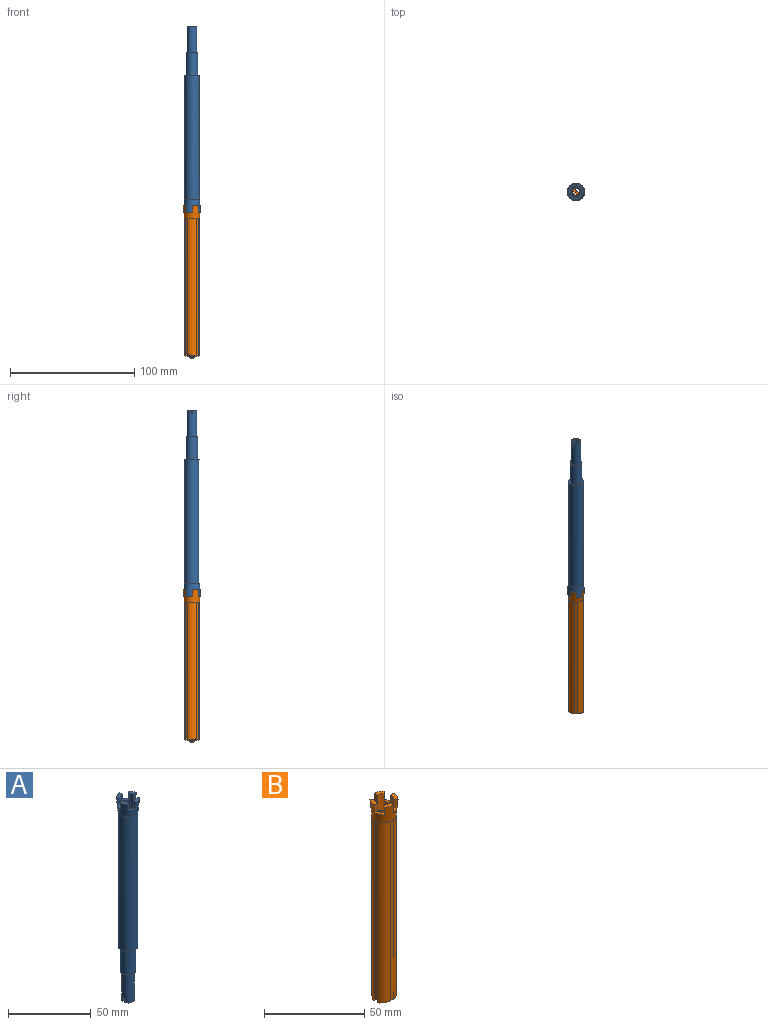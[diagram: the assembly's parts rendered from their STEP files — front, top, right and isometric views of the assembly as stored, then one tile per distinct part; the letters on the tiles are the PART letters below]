
ASSEMBLY  parts=2 mates=1
PART A: 37 faces, bbox 14x14x149.7 mm
  f0: plane 4.95x3.68mm, normal (0,0,1), area 10.6mm2, adj f3,f23,f26,f34
  f1: plane 4.96x3.68mm, normal (0,0,1), area 10.6mm2, adj f3,f23,f31,f35
  f2: plane 4.95x3.68mm, normal (0,0,1), area 10.6mm2, adj f3,f23,f28,f32
  f3: cylinder r=4.7mm len=108mm, axis (0,0,1), area 3115.5mm2, adj f0,f1,f2,f14,f24,f25,f26,f27
  f4: plane 7.63x3.1mm, normal (0,0,-1), area 8.3mm2, adj f9,f11,f16,f17
  f5: cylinder r=3.7mm len=14.3mm, axis (0,0,1), area 332.4mm2, adj f6,f14
  f6: cone r=3mm half-angle=9.9deg, axis (0,0,1), area 85.5mm2, adj f5,f11
  f7: cylinder r=4.7mm len=18.3mm, axis (0,0,-1), area 540.4mm2, adj f8,f13
  f8: plane 9.4x9.4mm, normal (0,0,-1), area 21.6mm2, adj f7,f9
  f9: cylinder r=3.9mm len=21.35mm, axis (0,0,1), area 514.1mm2, adj f4,f8,f10,f15,f16,f17,f18,f19
  f10: plane 7.63x3.1mm, normal (0,0,-1), area 8.3mm2, adj f9,f11,f15,f18
  f11: cylinder r=3mm len=19.35mm, axis (0,0,-1), area 355.6mm2, adj f4,f6,f10,f15,f16,f17,f18,f19
  f12: cylinder r=6mm len=100mm, axis (0,0,-1), area 3769.9mm2, adj f13,f23
  f13: plane 12x12mm, normal (0,0,-1), area 43.7mm2, adj f7,f12
  f14: revolved ~9.36x9.36mm, area 0mm2, adj f3,f5
  f15: plane 2.2x0.93mm, normal (0,-1,0), area 2mm2, adj f9,f10,f11,f19
  f16: plane 2.2x0.93mm, normal (0,1,0), area 2mm2, adj f4,f9,f11,f20
  f17: plane 2.2x0.93mm, normal (0,1,0), area 2mm2, adj f4,f9,f11,f21
  f18: plane 2.2x0.93mm, normal (0,-1,0), area 2mm2, adj f9,f10,f11,f22
  f19: cylinder r=0.8mm len=1.01mm, axis (-1,0,0), area 1.1mm2, adj f9,f11,f15,f20
  f20: cylinder r=0.8mm len=1.01mm, axis (-1,0,0), area 1.1mm2, adj f9,f11,f16,f19
  f21: cylinder r=0.8mm len=1.01mm, axis (-1,0,0), area 1.1mm2, adj f9,f11,f17,f22
  f22: cylinder r=0.8mm len=1.01mm, axis (-1,0,0), area 1.1mm2, adj f9,f11,f18,f21
  f23: cone r=6mm half-angle=5.7deg, axis (0,0,1), area 303.9mm2, adj f0,f1,f2,f12,f24,f25,f26,f27
  f24: plane 4.95x3.68mm, normal (0,0,1), area 10.6mm2, adj f3,f23,f25,f29
  f25: plane 5x2.3mm, normal (1,0,0), area 10.2mm2, adj f3,f23,f24,f27
  f26: plane 5x1.63mm, normal (-0.71,0.71,0), area 10.2mm2, adj f0,f3,f23,f27
  f27: plane 4.6x3.18mm, normal (0,0,1), area 7.9mm2, adj f3,f23,f25,f26
  f28: plane 5x2.3mm, normal (0,1,0), area 10.2mm2, adj f2,f3,f23,f30
  f29: plane 5x1.63mm, normal (-0.71,-0.71,0), area 10.2mm2, adj f3,f23,f24,f30
  f30: plane 4.6x3.18mm, normal (0,0,1), area 7.9mm2, adj f3,f23,f28,f29
  f31: plane 5x2.3mm, normal (-1,0,0), area 10.2mm2, adj f1,f3,f23,f33
  f32: plane 5x1.63mm, normal (0.71,-0.71,0), area 10.2mm2, adj f2,f3,f23,f33
  f33: plane 4.6x3.18mm, normal (0,0,1), area 7.9mm2, adj f3,f23,f31,f32
  f34: plane 5x2.3mm, normal (0,-1,0), area 10.2mm2, adj f0,f3,f23,f36
  f35: plane 5x1.63mm, normal (0.71,0.71,0), area 10.2mm2, adj f1,f3,f23,f36
  f36: plane 4.6x3.18mm, normal (0,0,1), area 7.9mm2, adj f3,f23,f34,f35
PART B: 67 faces, bbox 14x14x122.4 mm
  f0: plane 4.95x3.68mm, normal (0,0,1), area 10.6mm2, adj f47,f53,f56,f64
  f1: plane 4.95x3.68mm, normal (0,0,1), area 10.6mm2, adj f47,f53,f61,f65
  f2: plane 4.95x3.68mm, normal (0,0,1), area 10.6mm2, adj f47,f53,f58,f62
  f3: plane 110.33x0.31mm, normal (0,-1,0), area 33.9mm2, adj f18,f29,f46,f54
  f4: plane 110.33x0.6mm, normal (0,1,0), area 66.2mm2, adj f12,f26,f40,f54
  f5: plane 110.33x0.6mm, normal (0,1,0), area 66.2mm2, adj f12,f25,f40,f54
  f6: plane 109.6x2mm, normal (-1,0,0), area 219.2mm2, adj f16,f23,f33,f49
  f7: plane 111.13x7.75mm, normal (0,1,0), area 854.8mm2, adj f9,f17,f21,f32,f33,f35,f36,f54
  f8: plane 111.13x7.75mm, normal (0,-1,0), area 854.8mm2, adj f11,f27,f28,f32,f33,f35,f36,f54
  f9: plane 3.79x0.03mm, normal (0,0.26,-0.97), area 0.1mm2, adj f7,f10,f32,f35
  f10: cylinder r=1mm len=3.79mm, axis (1,0,0), area 13.9mm2, adj f9,f11,f32,f35
  f11: plane 3.79x0.03mm, normal (0,-0.26,-0.97), area 0.1mm2, adj f8,f10,f32,f35
  f12: plane 11.62x4.41mm, normal (0,-0.26,-0.97), area 25.7mm2, adj f4,f5,f22,f23,f24,f25,f26,f27
  f13: plane 109.6x2mm, normal (1,0,0), area 219.2mm2, adj f14,f22,f36,f51
  f14: cylinder r=6mm len=111.01mm, axis (0,0,-1), area 818.1mm2, adj f13,f15,f29,f37,f44,f47
  f15: plane 109.81x2mm, normal (0,1,0), area 219.6mm2, adj f14,f16,f29,f50
  f16: cylinder r=6mm len=111.01mm, axis (0,0,-1), area 818.1mm2, adj f6,f15,f29,f30,f43,f47
  f17: cylinder r=4mm len=111.01mm, axis (0,0,-1), area 471.6mm2, adj f7,f18,f29,f30,f43,f54
  f18: plane 110.36x0.13mm, normal (1,0,0), area 14mm2, adj f3,f17,f29,f54
  f19: plane 110.33x0.31mm, normal (0,-1,0), area 33.9mm2, adj f20,f29,f45,f54
  f20: plane 110.36x0.13mm, normal (-1,0,0), area 14mm2, adj f19,f21,f29,f54
  f21: cylinder r=4mm len=111.01mm, axis (0,0,-1), area 471.6mm2, adj f7,f20,f29,f37,f44,f54
  f22: cylinder r=6mm len=111.01mm, axis (0,0,-1), area 818.1mm2, adj f12,f13,f24,f34,f41,f47
  f23: cylinder r=6mm len=111.01mm, axis (0,0,-1), area 818.1mm2, adj f6,f12,f24,f31,f42,f47
  f24: plane 109.81x2mm, normal (0,-1,0), area 219.6mm2, adj f12,f22,f23,f52
  f25: plane 110.36x0.13mm, normal (-1,0,0), area 14mm2, adj f5,f12,f28,f54
  f26: plane 110.36x0.13mm, normal (1,0,0), area 14mm2, adj f4,f12,f27,f54
  f27: cylinder r=4mm len=111.01mm, axis (0,0,-1), area 471.6mm2, adj f8,f12,f26,f31,f42,f54
  f28: cylinder r=4mm len=111.01mm, axis (0,0,-1), area 471.6mm2, adj f8,f12,f25,f34,f41,f54
  f29: plane 11.62x4.41mm, normal (0,0.26,-0.97), area 25.7mm2, adj f3,f14,f15,f16,f17,f18,f19,f20
  f30: plane 2.04x1.01mm, normal (0,-1,0), area 2.1mm2, adj f16,f17,f33,f43
  f31: plane 2.04x1.01mm, normal (0,1,0), area 2.1mm2, adj f23,f27,f33,f42
  f32: plane 2.8x2mm, normal (-1,0,0), area 4mm2, adj f7,f8,f9,f10,f11,f33,f38
  f33: plane 4.02x2mm, normal (0,0,-1), area 8mm2, adj f6,f7,f8,f30,f31,f32
  f34: plane 2.04x1.01mm, normal (0,1,0), area 2.1mm2, adj f22,f28,f36,f41
  f35: plane 2.8x2mm, normal (1,0,0), area 4mm2, adj f7,f8,f9,f10,f11,f36,f38
  f36: plane 4.02x2mm, normal (0,0,-1), area 8mm2, adj f7,f8,f13,f34,f35,f37
  f37: plane 2.04x1.01mm, normal (0,-1,0), area 2.1mm2, adj f14,f21,f36,f44
  f38: cylinder r=0.6mm len=3.79mm, axis (1,0,0), area 14.3mm2, adj f32,f35
  f39: cylinder r=0.4mm len=110.27mm, axis (0,0,1), area 92.4mm2, adj f29,f45,f46,f54
  f40: cylinder r=0.4mm len=110.33mm, axis (0,0,1), area 138.6mm2, adj f4,f5,f12,f54
  f41: cylinder r=0.4mm len=2.21mm, axis (1,0,0), area 1.5mm2, adj f12,f22,f28,f34
  f42: cylinder r=0.4mm len=2.21mm, axis (1,0,0), area 1.5mm2, adj f12,f23,f27,f31
  f43: cylinder r=0.4mm len=2.21mm, axis (-1,0,0), area 1.5mm2, adj f16,f17,f29,f30
  f44: cylinder r=0.4mm len=2.21mm, axis (-1,0,0), area 1.5mm2, adj f14,f21,f29,f37
  f45: cylinder r=0.4mm len=110.33mm, axis (0,0,1), area 46.2mm2, adj f19,f29,f39,f54
  f46: cylinder r=0.4mm len=110.33mm, axis (0,0,1), area 46.2mm2, adj f3,f29,f39,f54
  f47: cone r=6mm half-angle=5.7deg, axis (0,0,1), area 303.9mm2, adj f0,f1,f2,f14,f16,f22,f23,f48
  f48: plane 4.95x3.68mm, normal (0,0,1), area 10.6mm2, adj f47,f53,f55,f59
  f49: plane 2x0.08mm, normal (0,0,-1), area 0.1mm2, adj f6,f47
  f50: plane 2x0.08mm, normal (0,0,-1), area 0.1mm2, adj f15,f47
  f51: plane 2x0.08mm, normal (0,0,-1), area 0.1mm2, adj f13,f47
  f52: plane 2x0.08mm, normal (0,0,-1), area 0.1mm2, adj f24,f47
  f53: cylinder r=4.7mm len=10mm, axis (0,0,1), area 221.5mm2, adj f0,f1,f2,f48,f54,f55,f56,f57
  f54: plane 9.4x9.4mm, normal (0,0,1), area 34.3mm2, adj f3,f4,f5,f7,f8,f17,f18,f19
  f55: plane 5x2.3mm, normal (-1,0,0), area 10.2mm2, adj f47,f48,f53,f57
  f56: plane 5x1.63mm, normal (0.71,0.71,0), area 10.2mm2, adj f0,f47,f53,f57
  f57: plane 4.6x3.18mm, normal (0,0,1), area 7.9mm2, adj f47,f53,f55,f56
  f58: plane 5x2.3mm, normal (0,1,0), area 10.2mm2, adj f2,f47,f53,f60
  f59: plane 5x1.63mm, normal (0.71,-0.71,0), area 10.2mm2, adj f47,f48,f53,f60
  f60: plane 4.6x3.18mm, normal (0,0,1), area 7.9mm2, adj f47,f53,f58,f59
  f61: plane 5x2.3mm, normal (1,0,0), area 10.2mm2, adj f1,f47,f53,f63
  f62: plane 5x1.63mm, normal (-0.71,-0.71,0), area 10.2mm2, adj f2,f47,f53,f63
  f63: plane 4.6x3.18mm, normal (0,0,1), area 7.9mm2, adj f47,f53,f61,f62
  f64: plane 5x2.3mm, normal (0,-1,0), area 10.2mm2, adj f0,f47,f53,f66
  f65: plane 5x1.63mm, normal (-0.71,0.71,0), area 10.2mm2, adj f1,f47,f53,f66
  f66: plane 4.6x3.18mm, normal (0,0,1), area 7.9mm2, adj f47,f53,f64,f65
PLACE A rot(axis=(1,0,0),180deg) t=(-62.52,69.45,189.49)mm
PLACE B rot(axis=(0,0,-1),45deg) t=(-62.52,69.45,0)mm
MATE cylindrical A.f3 <-> B.f14  axis (0,0,1) through (-62.52,69.45,121.19)mm
